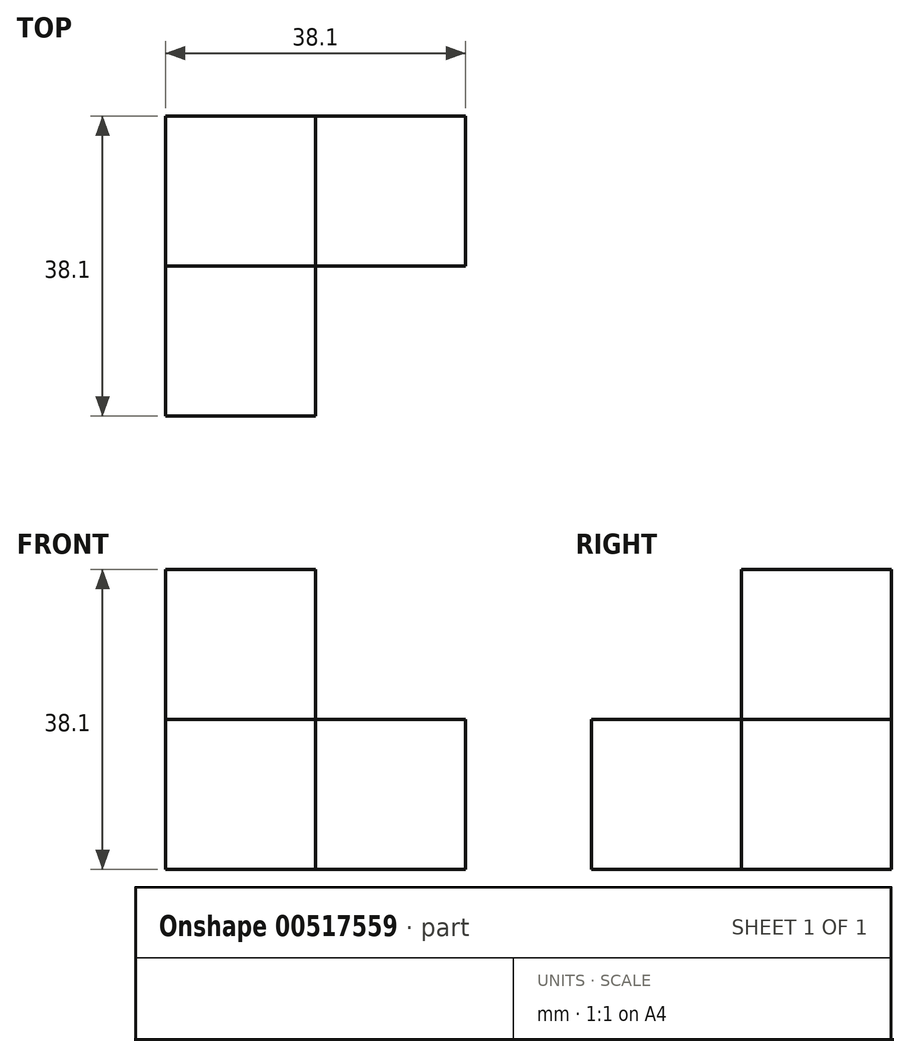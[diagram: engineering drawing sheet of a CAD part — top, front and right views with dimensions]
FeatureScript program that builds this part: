
annotation { "Feature Type Name" : "Feature", "Feature Type Description" : "" }
export const myFeature = defineFeature(function(context is Context, id is Id, definition is map)
    precondition{}
    {
        {
            var Q0;
            Q0=qCreatedBy(makeId("Front.planeOp"),FACE);
            var sketch = newSketch(context, id + "F0", { "sketchPlane" : qUnion([Q0])});
            skLineSegment(sketch, "E0.bottom", {"start": v(9.53, 9.52) * mm, "end": v(-9.53, 9.52) * mm});
            skLineSegment(sketch, "E0.top", {"start": v(9.53, -9.53) * mm, "end": v(-9.53, -9.53) * mm});
            skLineSegment(sketch, "E0.left", {"start": v(9.53, 9.52) * mm, "end": v(9.53, -9.53) * mm});
            skLineSegment(sketch, "E0.right", {"start": v(-9.53, 9.53) * mm, "end": v(-9.53, -9.53) * mm});
            skPoint(sketch, "E0.middle", {"position": v(0, 0) * mm});
            skLineSegment(sketch, "E1.bottom", {"start": v(-9.53, -9.53) * mm, "end": v(28.57, -9.53) * mm});
            skLineSegment(sketch, "E1.top", {"start": v(-9.53, -28.58) * mm, "end": v(28.57, -28.57) * mm});
            skLineSegment(sketch, "E1.left", {"start": v(-9.53, -9.53) * mm, "end": v(-9.53, -28.58) * mm});
            skLineSegment(sketch, "E1.right", {"start": v(28.57, -9.52) * mm, "end": v(28.58, -28.57) * mm});
            skSolve(sketch);
        }
        {
            var Q0;
            Q0 = qSketchRegion(id + "F0", true);
            extrude(context, id + "F1", {"entities" : qUnion([Q0]), "depth" : 19.05 * mm, "offsetDistance" : 25.4 * mm});
        }
        {
            var Q0;
            Q0=makeQuery(id+"F1.opExtrude","CAP_FACE",FACE,{"disambiguationData":[OSD([sQuery(id+"F0.wireOp",EDGE,"E0.bottom"),sQuery(id+"F0.wireOp",EDGE,"E0.left"),sQuery(id+"F0.wireOp",EDGE,"E0.right"),sQuery(id+"F0.wireOp",EDGE,"E1.bottom"),sQuery(id+"F0.wireOp",EDGE,"E1.top"),sQuery(id+"F0.wireOp",EDGE,"E1.left"),sQuery(id+"F0.wireOp",EDGE,"E1.right")])],"isStart":false});
            var sketch = newSketch(context, id + "F2", { "sketchPlane" : qUnion([Q0])});
            skLineSegment(sketch, "E2.bottom", {"start": v(-9.53, -28.58) * mm, "end": v(9.53, -28.58) * mm});
            skLineSegment(sketch, "E2.top", {"start": v(-9.53, -9.53) * mm, "end": v(9.53, -9.53) * mm});
            skLineSegment(sketch, "E2.left", {"start": v(-9.53, -28.58) * mm, "end": v(-9.53, -9.53) * mm});
            skLineSegment(sketch, "E2.right", {"start": v(9.53, -28.58) * mm, "end": v(9.53, -9.53) * mm});
            skSolve(sketch);
        }
        {
            var Q0;
            Q0=makeQuery(id+"F2.imprint","IMPRINT",FACE,{"disambiguationData":[TD([[makeQuery(id+"F2.imprint","IMPRINT",EDGE,{"derivedFrom":sQuery(id+"F2.wireOp",EDGE,"E2.bottom")}),1.0]])]});
            extrude(context, id + "F3", {"entities" : qUnion([Q0]), "operationType" : NewBodyOperationType.ADD, "depth" : 19.05 * mm, "offsetDistance" : 25.4 * mm});
        }
    });
